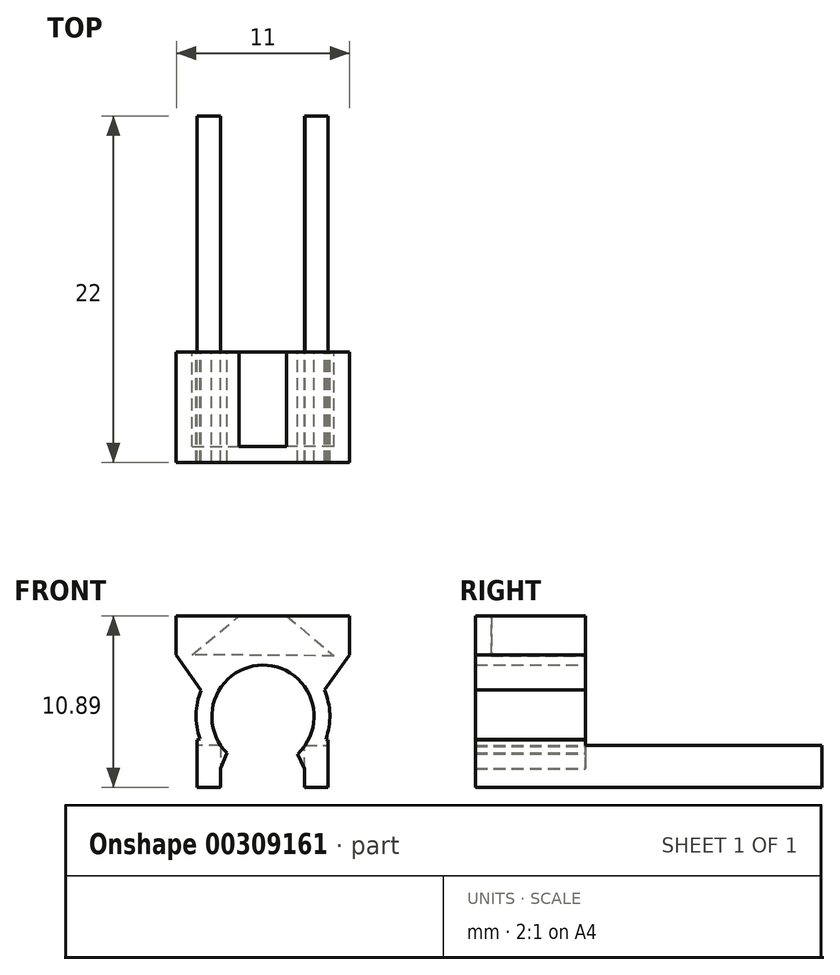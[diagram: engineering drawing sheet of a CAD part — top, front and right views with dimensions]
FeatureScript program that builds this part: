
annotation { "Feature Type Name" : "Feature", "Feature Type Description" : "" }
export const myFeature = defineFeature(function(context is Context, id is Id, definition is map)
    precondition{}
    {
        {
            var Q0;
            Q0=qCreatedBy(makeId("Front.planeOp"),FACE);
            var sketch = newSketch(context, id + "F0", { "sketchPlane" : qUnion([Q0])});
            skLineSegment(sketch, "E0", {"start": v(-3.34, -1.59) * mm, "end": v(-3.32, -1.6) * mm});
            skLineSegment(sketch, "E1", {"start": v(-3.32, -1.6) * mm, "end": v(-3.32, -2.3) * mm});
            skLineSegment(sketch, "E2", {"start": v(-3.32, -4.96) * mm, "end": v(-2.6, -4.96) * mm});
            skLineSegment(sketch, "E3", {"start": v(3.45, -1.64) * mm, "end": v(3.45, -2.3) * mm});
            skLineSegment(sketch, "E4", {"start": v(-4.1, -1.95) * mm, "end": v(-4.1, -4.96) * mm});
            skLineSegment(sketch, "E5", {"start": v(-4.1, -4.96) * mm, "end": v(-3.32, -4.96) * mm});
            skLineSegment(sketch, "E6.MirrorCS", {"start": v(4.22, -1.95) * mm, "end": v(4.22, -4.96) * mm});
            skLineSegment(sketch, "E7", {"start": v(-4.1, -1.95) * mm, "end": v(-3.32, -1.6) * mm});
            skLineSegment(sketch, "E8", {"start": v(4.22, -1.95) * mm, "end": v(3.45, -1.64) * mm});
            skLineSegment(sketch, "E9", {"start": v(0.1, 3.43) * mm, "end": v(-4.4, 3.47) * mm});
            skLineSegment(sketch, "E10", {"start": v(0.1, 3.43) * mm, "end": v(4.6, 3.4) * mm});
            skLineSegment(sketch, "E11", {"start": v(0.1, 3.43) * mm, "end": v(0.1, 5.93) * mm, "construction": true});
            skLineSegment(sketch, "E12", {"start": v(-4.4, 3.47) * mm, "end": v(-1.41, 5.93) * mm});
            skLineSegment(sketch, "E13", {"start": v(1.6, 5.93) * mm, "end": v(4.6, 3.4) * mm});
            skLineSegment(sketch, "E14", {"start": v(-1.41, 5.93) * mm, "end": v(-5.41, 5.93) * mm});
            skLineSegment(sketch, "E15", {"start": v(-5.41, 5.93) * mm, "end": v(-5.41, 3.47) * mm});
            skLineSegment(sketch, "E16", {"start": v(-5.41, 3.47) * mm, "end": v(-3.48, 0.71) * mm});
            skLineSegment(sketch, "E17", {"start": v(1.6, 5.93) * mm, "end": v(5.59, 5.93) * mm});
            skLineSegment(sketch, "E18", {"start": v(5.59, 5.93) * mm, "end": v(5.59, 3.47) * mm});
            skLineSegment(sketch, "E19", {"start": v(5.59, 3.47) * mm, "end": v(3.6, 0.71) * mm});
            skLineSegment(sketch, "E20", {"start": v(-1.41, 5.93) * mm, "end": v(1.6, 5.93) * mm});
            skLineSegment(sketch, "E21", {"start": v(-3.32, -2.3) * mm, "end": v(-4.1, -2.3) * mm});
            skLineSegment(sketch, "E22", {"start": v(3.45, -2.3) * mm, "end": v(4.22, -2.3) * mm});
            skLineSegment(sketch, "E23", {"start": v(3.45, -2.3) * mm, "end": v(3.45, -4.96) * mm, "construction": true});
            skLineSegment(sketch, "E24.0", {"start": v(2.72, -3.79) * mm, "end": v(2.72, -4.96) * mm});
            skLineSegment(sketch, "E25.0", {"start": v(-2.6, -2.3) * mm, "end": v(-2.6, -4.96) * mm});
            skLineSegment(sketch, "E26", {"start": v(-2.6, -2.3) * mm, "end": v(-3.32, -2.3) * mm});
            skPoint(sketch, "E27.orphan", {"position": v(2.25, -2.28) * mm});
            skPoint(sketch, "E28.orphan", {"position": v(-2.12, -2.28) * mm});
            skArc(sketch, "E29", {"start": v(-3.83, 1.2) * mm, "mid": v(-4.16, -0.32) * mm, "end": v(-3.91, -1.87) * mm});
            skArc(sketch, "E30.trimOffspring", {"start": v(4.08, -1.9) * mm, "mid": v(4.34, -0.32) * mm, "end": v(3.99, 1.25) * mm});
            skArc(sketch, "E31", {"start": v(2.28, -2.85) * mm, "mid": v(0.14, 2.8) * mm, "end": v(-2.18, -2.77) * mm});
            skLineSegment(sketch, "E32", {"start": v(2.72, -3.79) * mm, "end": v(2.28, -2.85) * mm});
            skLineSegment(sketch, "E33", {"start": v(-2.18, -2.77) * mm, "end": v(-2.6, -3.74) * mm});
            skLineSegment(sketch, "E34", {"start": v(3.45, -2.3) * mm, "end": v(2.77, -2.3) * mm});
            skLineSegment(sketch, "E35", {"start": v(2.72, -3.79) * mm, "end": v(2.72, -2.36) * mm});
            skLineSegment(sketch, "E36", {"start": v(2.72, -2.36) * mm, "end": v(2.77, -2.3) * mm});
            skLineSegment(sketch, "E37", {"start": v(2.72, -4.96) * mm, "end": v(4.22, -4.95) * mm});
            skSolve(sketch);
        }
        {
            var Q0;
            Q0=qSketchRegion(id+"F0",true);
            extrude(context, id + "F1", {"entities" : qUnion([Q0]), "depth" : 7 * mm});
        }
        {
            var Q0;
            Q0=makeQuery(id+"F0.imprint","IMPRINT",FACE,{"disambiguationData":[TD([[makeQuery(id+"F0.imprint","IMPRINT",EDGE,{"derivedFrom":sQuery(id+"F0.wireOp",EDGE,"E9")}),-1.0]])]});
            extrude(context, id + "F2", {"entities" : qUnion([Q0]), "operationType" : NewBodyOperationType.REMOVE, "depth" : 6 * mm});
        }
        {
            var Q0;
            Q0=makeQuery(id+"F0.imprint","IMPRINT",FACE,{"disambiguationData":[TD([[makeQuery(id+"F0.imprint","IMPRINT",EDGE,{"derivedFrom":sQuery(id+"F0.wireOp",EDGE,"f47f5537-e82d-4f6e-b3b4-383c7a984791")}),-1.0]])]});
            var Q1;
            Q1=makeQuery(id+"F0.imprint","IMPRINT",FACE,{"disambiguationData":[TD([[makeQuery(id+"F0.imprint","IMPRINT",EDGE,{"derivedFrom":sQuery(id+"F0.wireOp",EDGE,"E2")}),1.0]])]});
            var Q2;
            {var subQ0=sQuery(id+"F0.wireOp",EDGE,"E22");Q2=makeQuery(id+"F0.imprint","IMPRINT",FACE,{"disambiguationData":[TD([[makeQuery(id+"F0.imprint","IMPRINT",EDGE,{"derivedFrom":subQ0}),-1.0]])]});}
            extrude(context, id + "F3", {"entities" : qUnion([Q0, Q1, Q2]), "operationType" : NewBodyOperationType.ADD, "oppositeDirection" : true, "depth" : 15 * mm, "offsetDistance" : 25 * mm});
        }
    });
